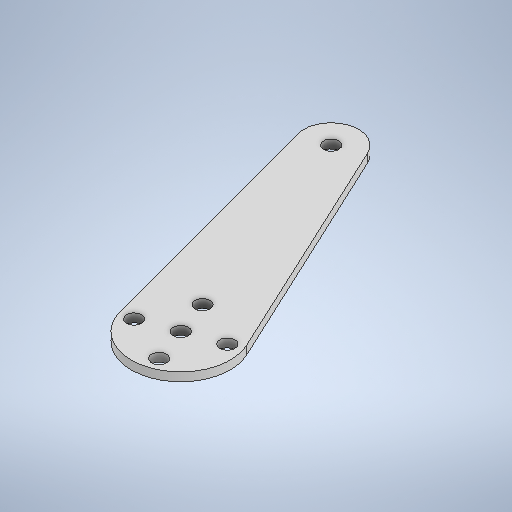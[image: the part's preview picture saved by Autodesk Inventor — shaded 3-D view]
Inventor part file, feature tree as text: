
AUTODESK INVENTOR PART (.ipt)
format: ipt  version: 2025.2 (Build 292293000, 293)  size: 284,672 bytes
history: native  units: in
note: dims shown in document units (in); Inventor stores cm internally (conversion verified against a paired STEP export)
features: extrude x2, sketch x2
ambient origin geometry x8: Origin, YZ Plane, XZ Plane, XY Plane, X Axis, Y Axis, Z Axis, Center Point
bodies: Solid1 (feature_tree)
feature tree (4):
  extrude  "Extrusion1"  Depth=0.0669in TaperAngle=0.0deg
  extrude  "Extrusion2"  Depth=0.0669in
  sketch  "Sketch1"  dims[d0=0.7731in d1=0.0669in d2=0.0in]
  sketch  "Sketch2"  dims[d3=0.2147in d4=0.1181in d5=0.1181in d6=0.1181in d7=0.1181in d12=0.1181in d13=0.1181in d18=1.9685in d19=0.2842in d20=0.2842in d21=0.2842in d22=0.2842in d23=0.0669in d24=0.0in]
